# Revit family: 32_MFX_MF5-medicare
name_source: partatom
category: Doors
revit_build: Autodesk Revit Architecture 2013 (Build: 20130531_2115(x64)
units: mm (PartAtom-declared; Revit-internal decimal feet)

## types (1)
- 32_MFX_MF5-medicare
    Analytic Construction = <None>
    Function = Interior
    Height = 2300 mm
    MFX_F_Door = 32_MFX_Door : Special handle-bowl
    MFX_F_Frame = 32_MFX_Frame : Corner protection double
    MFX_F_Hood = 32_MFX_Hood : Ceiling
    MFX_I_Fire rating = 0
    MFX_L_Free passing width = 1100 mm
    MFX_YN_Door in front of wall = No
    MFX_YN_Door self-closing = Yes
    MFX_YN_Rail motor on top = Yes
    Manufacturer = Metaflex
    Model = MF5-Medicare
    Rough Height = 2300 mm
    Rough Width = 1230 mm  [stored 4.03543 ft]
    Type Comments = Metaflex schuifdeur Medicare
    URL = www.metaflex.nl
    Wall Closure = By host
    Width = 1220 mm  [stored 4.00262 ft]

note: [stored X ft] marks values corroborated as IEEE doubles in the binary element streams (Revit-internal decimal feet)

## geometry (parser evidence)
native form markers: Blend x8, Sweep x8
no freeform markers — native parametric forms only
